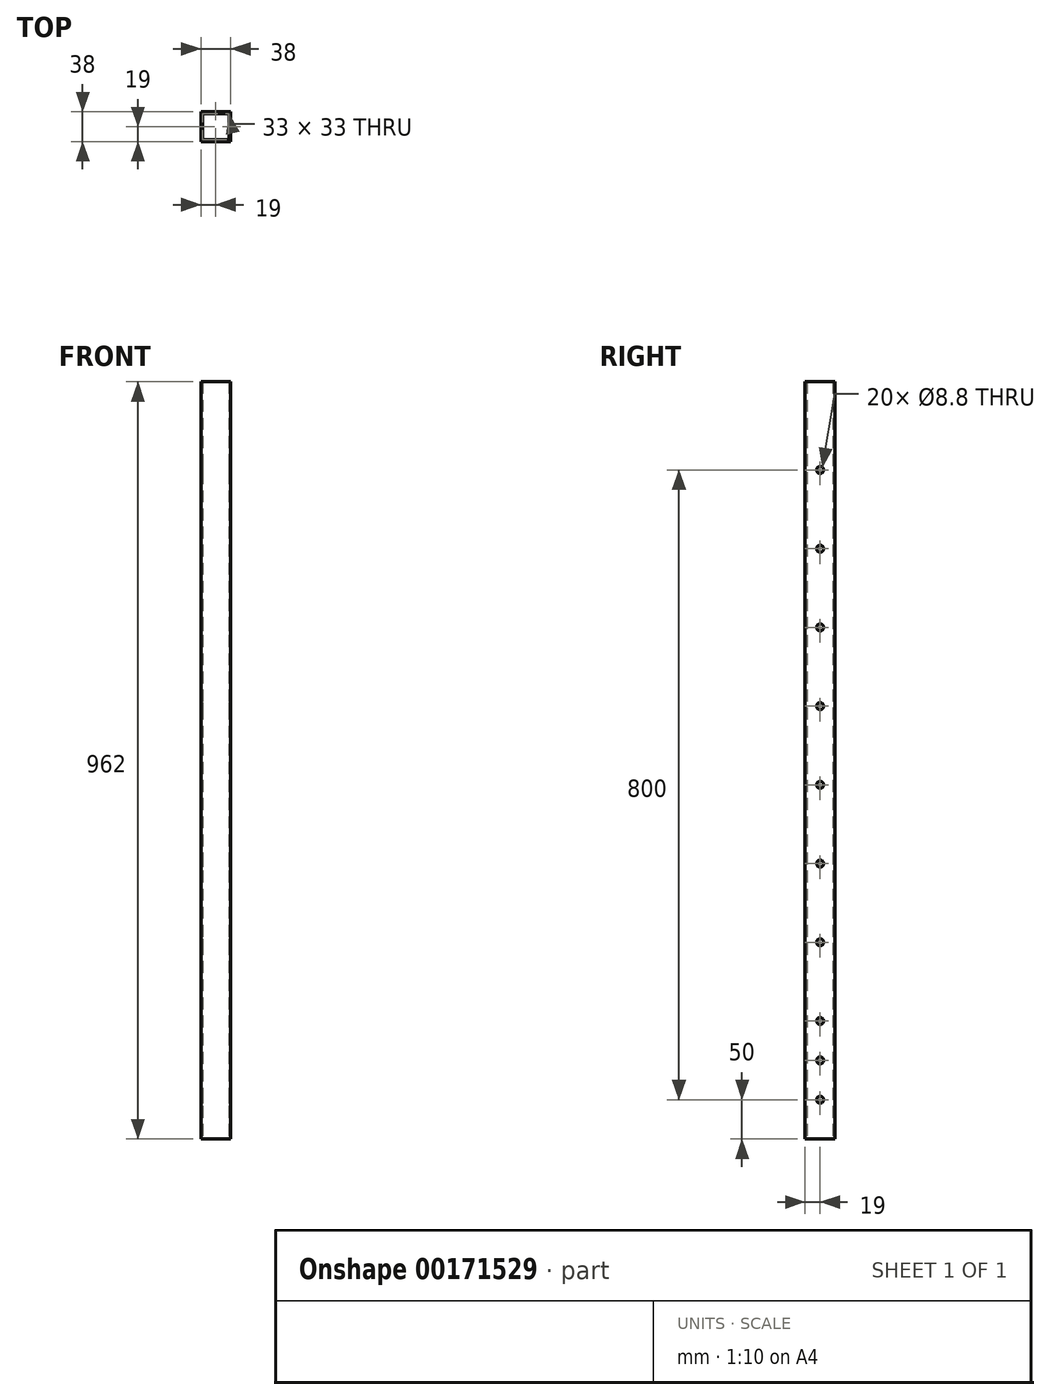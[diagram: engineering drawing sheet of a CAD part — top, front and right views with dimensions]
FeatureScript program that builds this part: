
annotation { "Feature Type Name" : "Feature", "Feature Type Description" : "" }
export const myFeature = defineFeature(function(context is Context, id is Id, definition is map)
    precondition{}
    {
        {
            var Q0;
            Q0=qCreatedBy(makeId("Top.planeOp"),FACE);
            var sketch = newSketch(context, id + "F0", { "sketchPlane" : qUnion([Q0])});
            skLineSegment(sketch, "E0.bottom", {"start": v(19, -19) * mm, "end": v(-19, -19) * mm});
            skLineSegment(sketch, "E0.top", {"start": v(19, 19) * mm, "end": v(-19, 19) * mm});
            skLineSegment(sketch, "E0.left", {"start": v(19, -19) * mm, "end": v(19, 19) * mm});
            skLineSegment(sketch, "E0.right", {"start": v(-19, -19) * mm, "end": v(-19, 19) * mm});
            skPoint(sketch, "E0.middle", {"position": v(0, 0) * mm});
            skLineSegment(sketch, "E1.bottom", {"start": v(16.5, -16.5) * mm, "end": v(-16.5, -16.5) * mm});
            skLineSegment(sketch, "E1.top", {"start": v(16.5, 16.5) * mm, "end": v(-16.5, 16.5) * mm});
            skLineSegment(sketch, "E1.left", {"start": v(16.5, -16.5) * mm, "end": v(16.5, 16.5) * mm});
            skLineSegment(sketch, "E1.right", {"start": v(-16.5, -16.5) * mm, "end": v(-16.5, 16.5) * mm});
            skSolve(sketch);
        }
        {
            var Q0;
            Q0=makeQuery(id+"F0.imprint","IMPRINT",FACE,{"disambiguationData":[TD([[makeQuery(id+"F0.imprint","IMPRINT",EDGE,{"derivedFrom":sQuery(id+"F0.wireOp",EDGE,"E0.bottom")}),-1.0]])]});
            extrude(context, id + "F1", {"entities" : qUnion([Q0]), "depth" : 962 * mm});
        }
        {
            var Q0;
            Q0=makeQuery(id+"F1.opExtrude","SWEPT_FACE",FACE,{"disambiguationData":[OSD([sQuery(id+"F0.wireOp",EDGE,"E0.right")])]});
            var sketch = newSketch(context, id + "F2", { "sketchPlane" : qUnion([Q0])});
            skPoint(sketch, "E2", {"position": v(0, 750) * mm});
            skPoint(sketch, "E2.positionSnap0", {"position": v(0, 962) * mm});
            skPoint(sketch, "E3", {"position": v(0, 650) * mm});
            skPoint(sketch, "E4", {"position": v(0, 550) * mm});
            skPoint(sketch, "E5", {"position": v(0, 50) * mm});
            skPoint(sketch, "E5.positionSnap0", {"position": v(0, 0) * mm});
            skPoint(sketch, "E6", {"position": v(0, 100) * mm});
            skPoint(sketch, "E7", {"position": v(0, 150) * mm});
            skPoint(sketch, "E8", {"position": v(0, 250) * mm});
            skPoint(sketch, "E9", {"position": v(0, 350) * mm});
            skPoint(sketch, "E10", {"position": v(0, 450) * mm});
            skPoint(sketch, "E11", {"position": v(0, 850) * mm});
            skSolve(sketch);
        }
        {
            var Q0;
            Q0=sQuery(id+"F2.wireOp",VERTEX,"E8");
            var Q1;
            Q1=sQuery(id+"F2.wireOp",VERTEX,"E9");
            var Q2;
            Q2=sQuery(id+"F2.wireOp",VERTEX,"E10");
            var Q3;
            Q3=sQuery(id+"F2.wireOp",VERTEX,"E7");
            var Q4;
            Q4=sQuery(id+"F2.wireOp",VERTEX,"E6");
            var Q5;
            Q5=sQuery(id+"F2.wireOp",VERTEX,"E5");
            var Q6;
            Q6=sQuery(id+"F2.wireOp",VERTEX,"E4");
            var Q7;
            Q7=sQuery(id+"F2.wireOp",VERTEX,"E2");
            var Q8;
            Q8=sQuery(id+"F2.wireOp",VERTEX,"E3");
            var Q9;
            Q9=sQuery(id+"F2.wireOp",VERTEX,"E11");
            var Q10;
            Q10=makeQuery(id+"F1.opExtrude","SWEPT_BODY",BODY,{"disambiguationData":[OSD([sQuery(id+"F0.wireOp",EDGE,"E0.bottom"),sQuery(id+"F0.wireOp",EDGE,"E0.top"),sQuery(id+"F0.wireOp",EDGE,"E0.left"),sQuery(id+"F0.wireOp",EDGE,"E0.right"),sQuery(id+"F0.wireOp",EDGE,"E1.bottom"),sQuery(id+"F0.wireOp",EDGE,"E1.top"),sQuery(id+"F0.wireOp",EDGE,"E1.left"),sQuery(id+"F0.wireOp",EDGE,"E1.right")])]});
            hole(context, id + "F3", {"style" : HoleStyle.SIMPLE, "endStyle" : HoleEndStyle.THROUGH, "standardTappedOrClearance" : lookupTablePath({ "standard" : "ISO", "fit" : "Normal", "size" : "M8", "type" : "Clearance" }), "standardBlindInLast" : lookupTablePath({ "fit" : "Standard", "standard" : "ISO", "size" : "M8", "type" : "Clearance" }), "holeDiameter" : 8.8 * mm, "locations" : qUnion([Q0, Q1, Q2, Q3, Q4, Q5, Q6, Q7, Q8, Q9]), "scope" : qUnion([Q10]), "isTappedThrough" : true});
        }
    });
